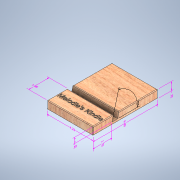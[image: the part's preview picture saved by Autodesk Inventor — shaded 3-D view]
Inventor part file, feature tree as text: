
AUTODESK INVENTOR PART (.ipt)
format: ipt  version: 2020.2 (Build 242310000, 310)  size: 422,400 bytes
history: native  units: in
note: dims shown in document units (in); Inventor stores cm internally (conversion verified against a paired STEP export)
features: other x8, extrude x3, sketch x3, fillet x1
ambient origin geometry x8: Origin, YZ Plane, XZ Plane, XY Plane, X Axis, Y Axis, Z Axis, Center Point
bodies: Solid1 (feature_tree)
feature tree (15):
  other  "Annotations"
  extrude  "Extrusion1"  Depth=6.0in
  extrude  "Extrusion3"  Depth=0.75in
  extrude  "Extrusion4"  TaperAngle=75.0deg  [1 undecoded]
  fillet  "Fillet1"  [1 undecoded]
  sketch  "Sketch2"  dims[d0=4.25in d1=6.0in]
  sketch  "Sketch4"  dims[d2=0.75in d3=0.0in d27=0.5in]
  sketch  "Sketch6"  dims[d28=1.75in d29=75.0deg d31=0.0in d32=0.0in d46=0.5in d50=1.0in d51=0.1in d52=0.0in d53=0.0625in d10=0.0949in d11=4.25in d12=0.3164in d13=0.1734in d14=6.0in d33=0.1905in d34=0.5in d35=0.2828in d36=0.1784in d37=0.75in d41=0.1884in d42=1.75in d43=0.314in d44=0.0802in d45=1.884in d47=0.2389in d48=0.113in d49=75.0deg d9=0.1629in]
  other  "Linear Dimension 1"
  other  "Linear Dimension 2"
  other  "Linear Dimension 3"
  other  "Linear Dimension 4"
  other  "Linear Dimension 5"
  other  "Linear Dimension 6"
  other  "Angular Dimension 1"
note: 2 required parameter values undecoded (feature->parameter linkage not recoverable at this tier; creation-order binding heuristic only, values carry confidence <= 0.55)
